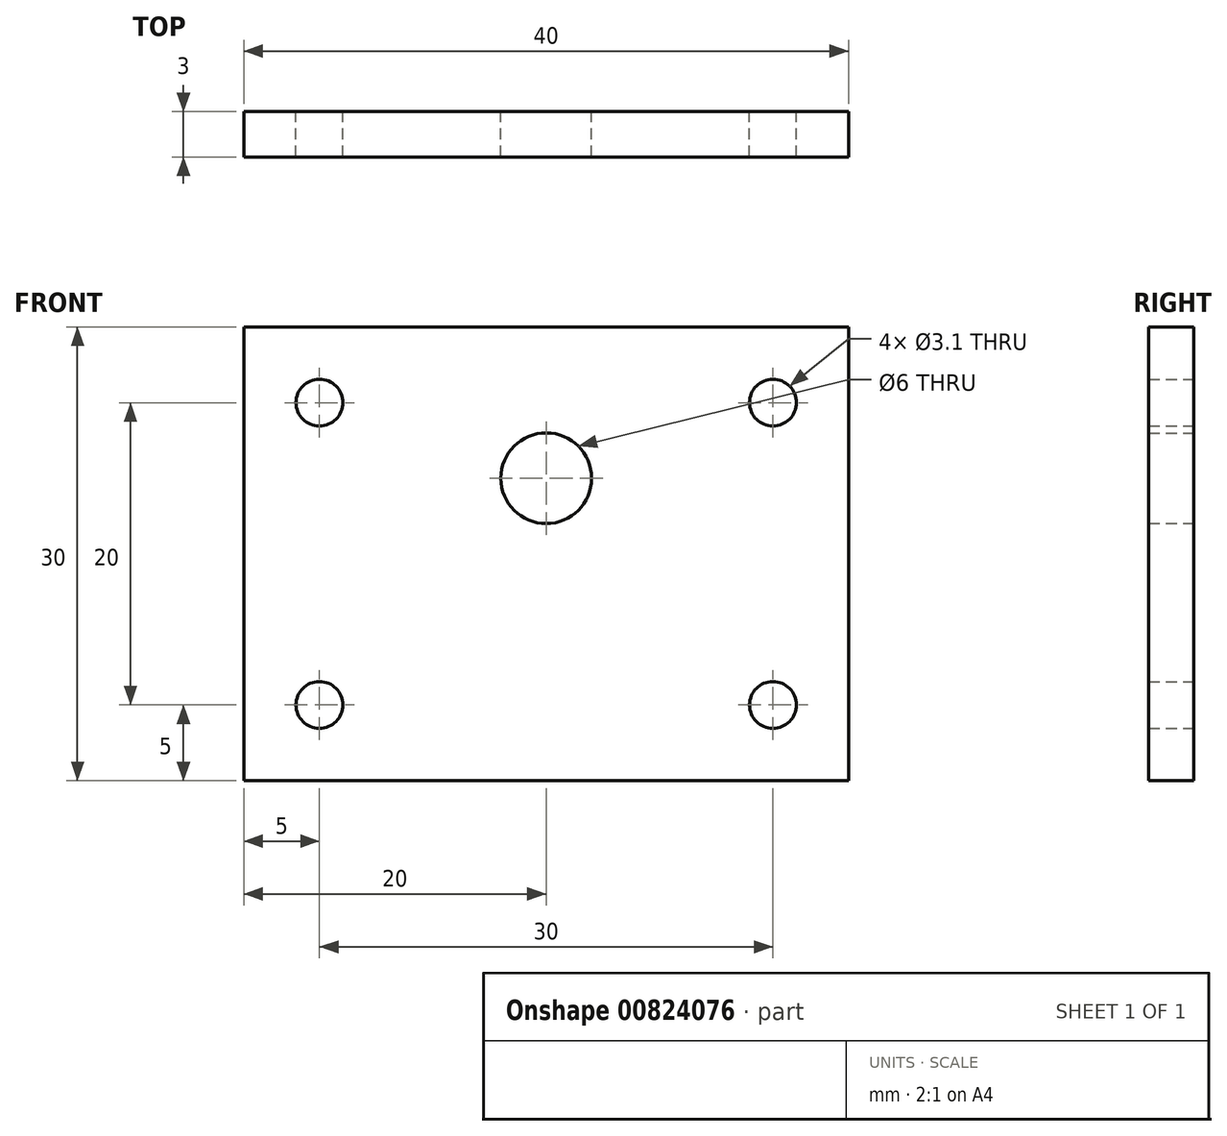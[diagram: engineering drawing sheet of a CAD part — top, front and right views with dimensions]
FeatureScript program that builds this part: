
annotation { "Feature Type Name" : "Feature", "Feature Type Description" : "" }
export const myFeature = defineFeature(function(context is Context, id is Id, definition is map)
    precondition{}
    {
        {
            var Q0;
            Q0=qCreatedBy(makeId("Front.planeOp"),FACE);
            var sketch = newSketch(context, id + "F0", { "sketchPlane" : qUnion([Q0])});
            skLineSegment(sketch, "E0.bottom", {"start": v(20, -15) * mm, "end": v(-20, -15) * mm});
            skLineSegment(sketch, "E0.top", {"start": v(20, 15) * mm, "end": v(-20, 15) * mm});
            skLineSegment(sketch, "E0.left", {"start": v(20, -15) * mm, "end": v(20, 15) * mm});
            skLineSegment(sketch, "E0.right", {"start": v(-20, -15) * mm, "end": v(-20, 15) * mm});
            skPoint(sketch, "E0.middle", {"position": v(0, 0) * mm});
            skCircle(sketch, "E1", {"center": v(0, 5) * mm, "radius": 3 * mm});
            skCircle(sketch, "E2", {"center": v(15, 10) * mm, "radius": 1.55 * mm});
            skCircle(sketch, "E3.MirrorC", {"center": v(-15, 10) * mm, "radius": 1.55 * mm});
            skCircle(sketch, "E4.MirrorC", {"center": v(15, -10) * mm, "radius": 1.55 * mm});
            skCircle(sketch, "E5.MirrorC", {"center": v(-15, -10) * mm, "radius": 1.55 * mm});
            skSolve(sketch);
        }
        {
            var Q0;
            Q0 = qSketchRegion(id + "F0", true);
            extrude(context, id + "F1", {"entities" : qUnion([Q0]), "depth" : 3 * mm, "offsetDistance" : 25 * mm});
        }
    });
